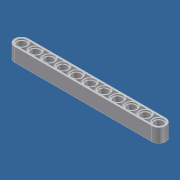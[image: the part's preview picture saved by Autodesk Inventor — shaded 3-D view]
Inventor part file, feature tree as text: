
AUTODESK INVENTOR PART (.ipt)
format: ipt  version: unknown  size: 352,256 bytes
history: native  units: mm
features: extrude x5, sketch x5
ambient origin geometry x8: Origin, YZ Plane, XZ Plane, XY Plane, X Axis, Y Axis, Z Axis, Center Point
bodies: Solid1 (feature_tree)
feature tree (10):
  extrude  "Extrusion1"  Depth=4.0mm
  extrude  "Extrusion18"  TaperAngle=0.0deg  [1 undecoded]
  extrude  "Extrusion19"  TaperAngle=180.0deg  [1 undecoded]
  extrude  "Extrusion20"  Depth=8.0mm TaperAngle=0.0deg
  extrude  "Extrusion21"  Depth=5.0mm
  sketch  "Sketch2"  dims[d0=4.0mm d1=4.0mm]
  sketch  "Sketch19"  dims[d2=80.0mm d3=0.0mm]
  sketch  "Sketch20"  dims[d4=40.0mm d9=180.0deg]
  sketch  "Sketch21"  dims[d10=0.0mm d12=8.0mm d13=0.0mm]
  sketch  "Sketch22"  dims[d183=80.0mm d184=5.0mm d185=10.0mm d187=10.0mm d188=110.0mm d190=8.0mm d192=10.0mm d193=0.0mm d194=6.0mm d195=10.0mm d197=10.0mm d198=110.0mm d200=8.0mm d202=0.8mm d203=0.0mm d204=6.0mm d205=10.0mm d207=10.0mm d208=110.0mm d210=8.0mm d212=0.8mm d213=0.0mm d214=7.0mm d215=7.0mm d216=10.0mm d218=10.0mm d219=100.0mm d221=8.0mm d223=0.8mm d224=0.0mm]
note: 2 required parameter values undecoded (feature->parameter linkage not recoverable at this tier; creation-order binding heuristic only, values carry confidence <= 0.55)
